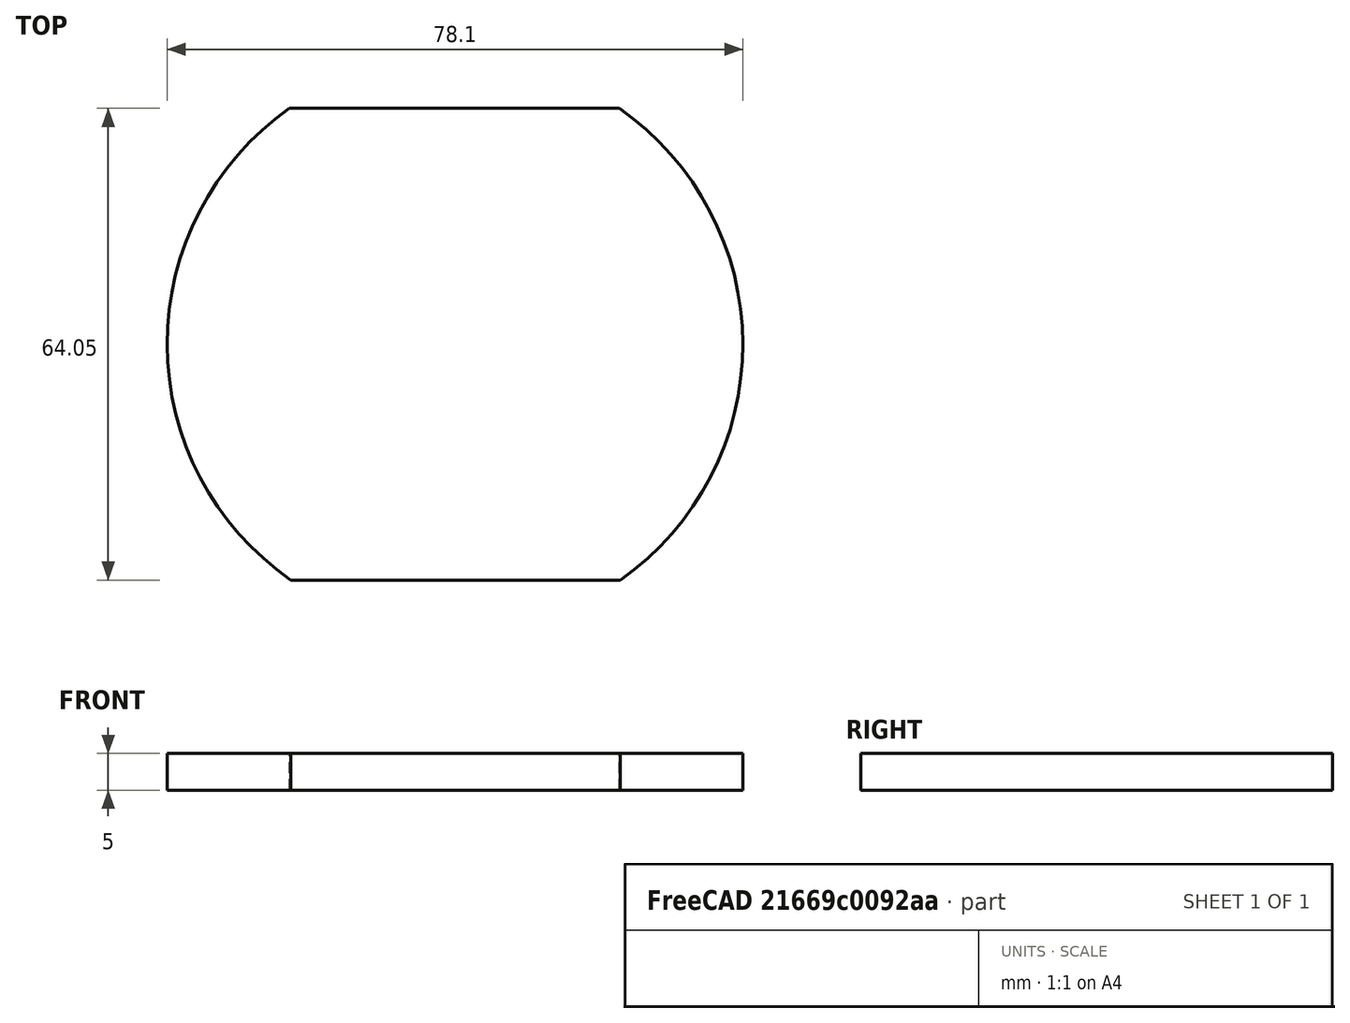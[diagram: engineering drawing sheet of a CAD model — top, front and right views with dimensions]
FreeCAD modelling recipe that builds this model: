
FCSTD DOCUMENT  (FreeCAD 1.0R39319 (Git))
Label: chapa_chord_cut_CLEAN
License: All rights reserved
LicenseURL: https://en.wikipedia.org/wiki/All_rights_reserved
objects: Sketcher::SketchObject×1, PartDesign::Pad×1, PartDesign::Body×1
note: 6 computed .brp shape members not serialized (recipe doc carries the construction recipe); baked Part::Feature solids carry a one-line shape summary decoded from their .brp

FEATURE [Sketcher::SketchObject] Sketch_1
  ArcFitTolerance = 1e-06
  AttachmentSupport = -> [XY_Plane]
  FullyConstrained = false
  MakeInternals = false
  MapMode = 5
  sketch-geometry (4):
    g0: ArcOfCircle CenterX=-0.00137376 CenterY=6.62548 CenterZ=0 NormalX=0 NormalY=0 NormalZ=1 AngleXU=0 Radius=39.0495 StartAngle=5.32436 EndAngle=7.24732
    g1: LineSegment StartX=22.262 StartY=38.7067 StartZ=0 EndX=-22.4508 EndY=38.7067 EndZ=0
    g2: ArcOfCircle CenterX=0.00220858 CenterY=6.7507 CenterZ=0 NormalX=0 NormalY=0 NormalZ=1 AngleXU=0 Radius=39.0554 StartAngle=2.18328 EndAngle=4.1058
    g3: LineSegment StartX=-22.262 StartY=-25.3372 StartZ=0 EndX=22.4319 EndY=-25.3372 EndZ=0
  constraints (7):
    c: Coincident(g0,g1)
    c: Coincident(g1,g2)
    c: Coincident(g2,g3)
    c: Coincident(g3,g0)
    c: Parallel(g1,g3)
    c: Horizontal(g1)
    c: Distance(g1,g3) = 78
FEATURE [PartDesign::Pad] Pad_1
  Direction = (0,0,1)
  Length = 5
  Length2 = 10
  Profile = -> Sketch_1
  Refine = true
  Suppressed = false
  Type = 0
FEATURE [PartDesign::Body] Body
  AllowCompound = false
  Group = -> [Sketch_1,Pad_1]
  Origin = -> Origin
  Tip = -> Pad_1
